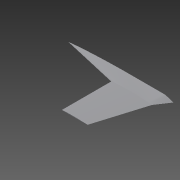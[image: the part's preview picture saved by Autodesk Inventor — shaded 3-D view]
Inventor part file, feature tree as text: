
AUTODESK INVENTOR PART (.ipt)
format: ipt  version: 2014 SP1 (Build 180222100, 222)  size: 187,904 bytes
history: native  units: mm
features: sketch x4, plane x3, loft x2, fillet x1, extrude x1, other x1
ambient origin geometry x8: Origin, YZ Plane, XZ Plane, XY Plane, X Axis, Y Axis, Z Axis, Center Point
bodies: Solid1 (feature_tree)
feature tree (12):
  sketch  "Sketch1"  dims[d0=490.0mm d11=60.0mm]
  plane  "Work Plane1"
  sketch  "Sketch2"  dims[d12=230.0mm d13=120.0mm d14=0.0mm d15=90.0deg]
  plane  "Work Plane2"
  loft  "Loft1"
  loft  "Loft2"
  plane  "Work Plane3"
  fillet  "Fillet1"  [1 undecoded]
  extrude  "Extrusion3"  TaperAngle=0.0deg  [1 undecoded]
  sketch  "Sketch3"  dims[d16=0.0mm d17=90.0deg d18=0.0mm d19=90.0deg]
  other  "Edges1"
  sketch  "Sketch5"  dims[d20=0.0mm d21=90.0deg d22=0.0mm d30=40.0mm d31=10.0mm d32=30.0mm d33=0.0mm]
note: 2 required parameter values undecoded (feature->parameter linkage not recoverable at this tier; creation-order binding heuristic only, values carry confidence <= 0.55)
